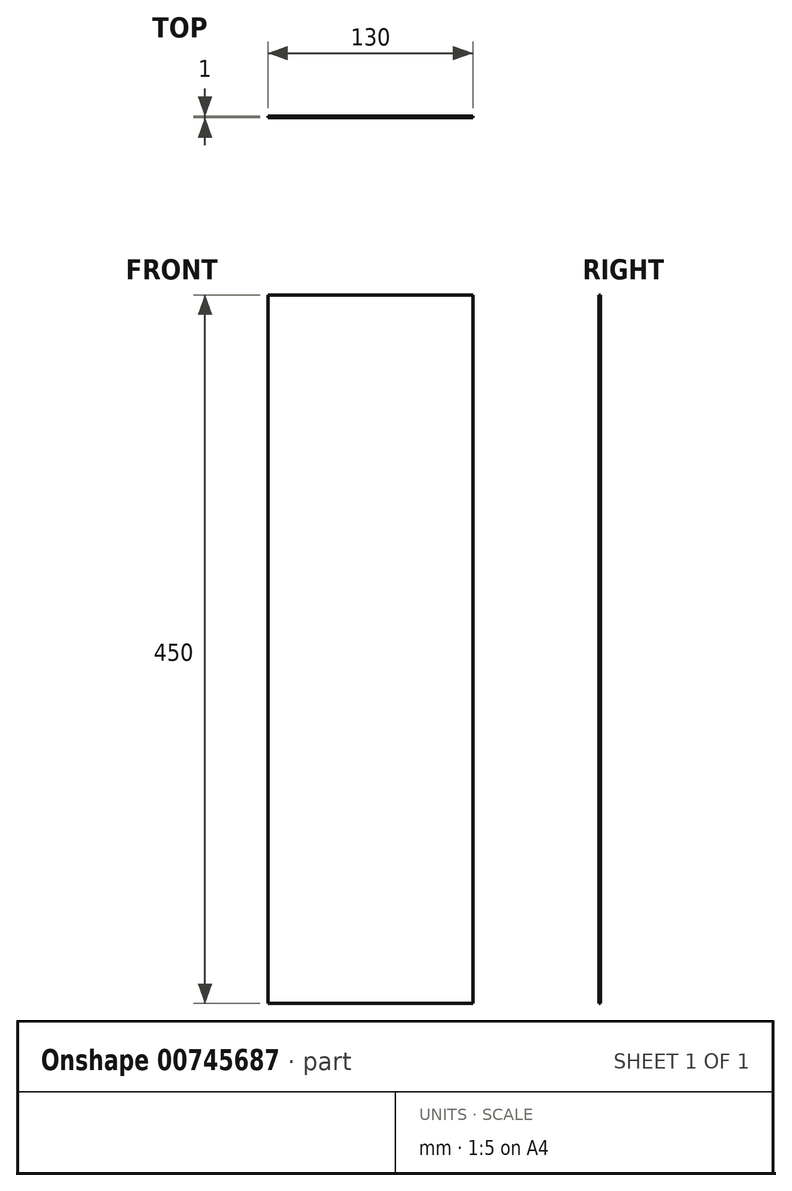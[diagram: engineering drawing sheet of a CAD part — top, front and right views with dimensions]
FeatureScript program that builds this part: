
annotation { "Feature Type Name" : "Feature", "Feature Type Description" : "" }
export const myFeature = defineFeature(function(context is Context, id is Id, definition is map)
    precondition{}
    {
        {
            var Q0;
            Q0=qCreatedBy(makeId("Front.planeOp"),FACE);
            var sketch = newSketch(context, id + "F0", { "sketchPlane" : qUnion([Q0])});
            skLineSegment(sketch, "E0.bottom", {"start": v(65, 225) * mm, "end": v(-65, 225) * mm});
            skLineSegment(sketch, "E0.top", {"start": v(65, -225) * mm, "end": v(-65, -225) * mm});
            skLineSegment(sketch, "E0.left", {"start": v(65, 225) * mm, "end": v(65, -225) * mm});
            skLineSegment(sketch, "E0.right", {"start": v(-65, 225) * mm, "end": v(-65, -225) * mm});
            skPoint(sketch, "E0.middle", {"position": v(0, 0) * mm});
            skSolve(sketch);
        }
        {
            var Q0;
            Q0=makeQuery(id+"F0.imprint","IMPRINT",FACE,{"disambiguationData":[TD([[makeQuery(id+"F0.imprint","IMPRINT",EDGE,{"derivedFrom":sQuery(id+"F0.wireOp",EDGE,"E0.bottom")}),1.0]])]});
            extrude(context, id + "F1", {"entities" : qUnion([Q0]), "depth" : 1 * mm, "offsetDistance" : 25.4 * mm});
        }
    });
